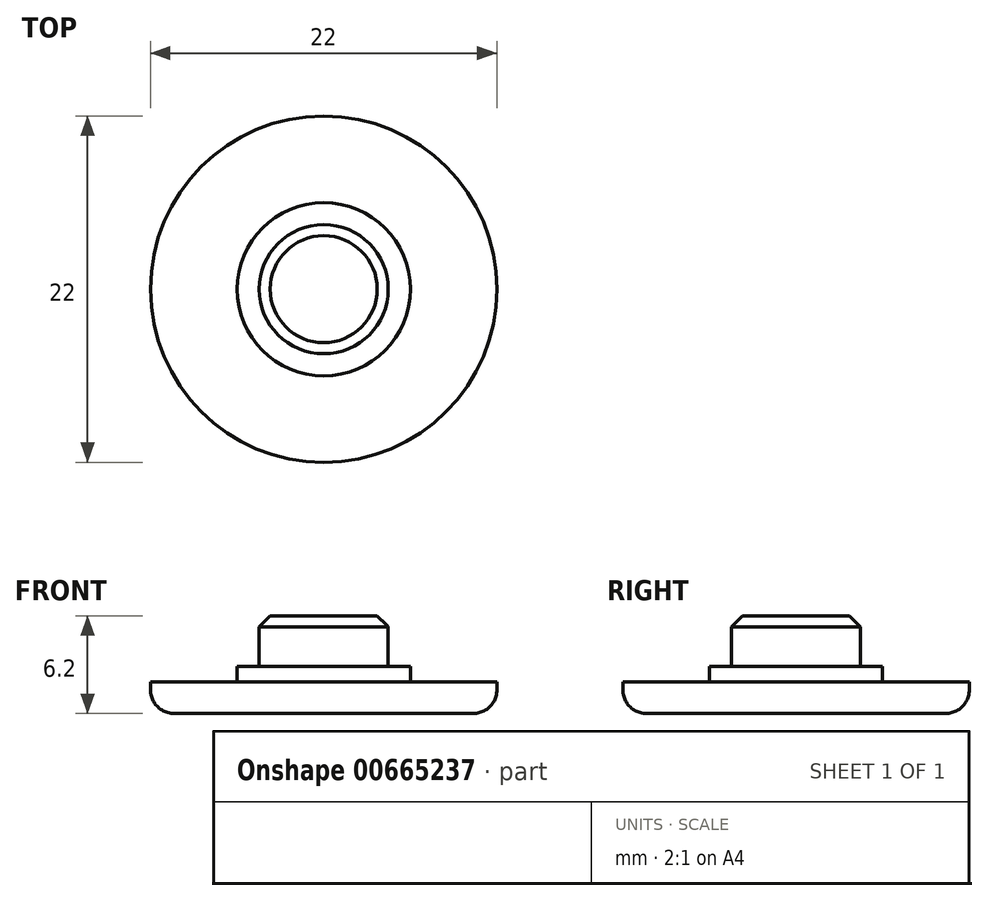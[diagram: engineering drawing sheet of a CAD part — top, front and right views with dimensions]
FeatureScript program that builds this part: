
annotation { "Feature Type Name" : "Feature", "Feature Type Description" : "" }
export const myFeature = defineFeature(function(context is Context, id is Id, definition is map)
    precondition{}
    {
        {
            var Q0;
            Q0=qCreatedBy(makeId("Top.planeOp"),FACE);
            var sketch = newSketch(context, id + "F0", { "sketchPlane" : qUnion([Q0])});
            skCircle(sketch, "E0", {"center": v(0, 0) * mm, "radius": 11 * mm});
            skSolve(sketch);
        }
        {
            var Q0;
            Q0 = qSketchRegion(id + "F0", true);
            extrude(context, id + "F1", {"entities" : qUnion([Q0]), "depth" : 2 * mm, "offsetDistance" : 25 * mm});
        }
        {
            var Q0;
            Q0=makeQuery(id+"F1.opExtrude","CAP_FACE",FACE,{"disambiguationData":[OSD([sQuery(id+"F0.wireOp",EDGE,"E0")])],"isStart":false});
            var sketch = newSketch(context, id + "F2", { "sketchPlane" : qUnion([Q0])});
            skCircle(sketch, "E1", {"center": v(0, 0) * mm, "radius": 5.5 * mm});
            skSolve(sketch);
        }
        {
            var Q0;
            Q0 = qSketchRegion(id + "F2", true);
            extrude(context, id + "F3", {"entities" : qUnion([Q0]), "operationType" : NewBodyOperationType.ADD, "depth" : 1 * mm, "offsetDistance" : 25 * mm});
        }
        {
            var Q0;
            Q0=makeQuery(id+"F3.opExtrude","CAP_FACE",FACE,{"disambiguationData":[OSD([sQuery(id+"F2.wireOp",EDGE,"E1")])],"isStart":false});
            var sketch = newSketch(context, id + "F4", { "sketchPlane" : qUnion([Q0])});
            skCircle(sketch, "E2", {"center": v(0, 0) * mm, "radius": 4.1 * mm});
            skSolve(sketch);
        }
        {
            var Q0;
            Q0 = qSketchRegion(id + "F4", true);
            extrude(context, id + "F5", {"entities" : qUnion([Q0]), "operationType" : NewBodyOperationType.ADD, "depth" : 3.2 * mm, "offsetDistance" : 25 * mm});
        }
        {
            var Q0;
            Q0=makeQuery(id+"F1.opExtrude","CAP_EDGE",EDGE,{"disambiguationData":[OSD([sQuery(id+"F0.wireOp",EDGE,"E0")])],"isStart":true});
            fillet(context, id + "F6", {"entities" : qUnion([Q0]), "radius" : 1.5 * mm, "tangentPropagation" : true, "allowEdgeOverflow" : false});
        }
        {
            var Q0;
            Q0=makeQuery(id+"F5.opExtrude","CAP_EDGE",EDGE,{"disambiguationData":[OSD([sQuery(id+"F4.wireOp",EDGE,"E2")])],"isStart":false});
            chamfer(context, id + "F7", {"entities" : qUnion([Q0]), "width" : .7 * mm, "tangentPropagation" : true});
        }
    });
